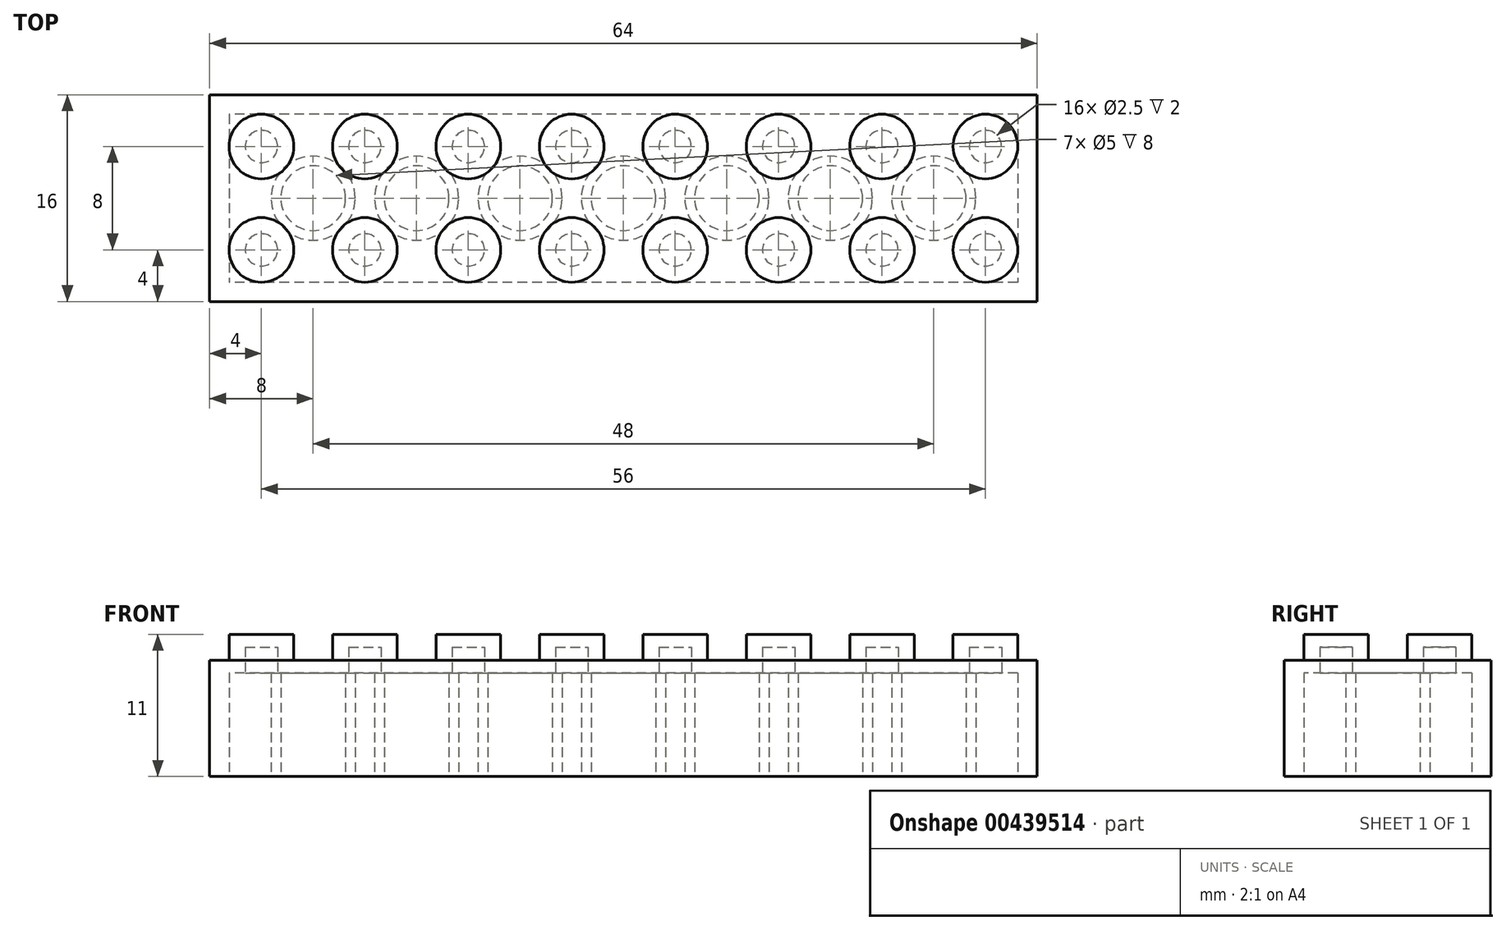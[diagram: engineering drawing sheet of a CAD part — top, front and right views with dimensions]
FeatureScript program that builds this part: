
annotation { "Feature Type Name" : "Feature", "Feature Type Description" : "" }
export const myFeature = defineFeature(function(context is Context, id is Id, definition is map)
    precondition{}
    {
        {
            var Q0;
            Q0=qCreatedBy(makeId("Top.planeOp"),FACE);
            var sketch = newSketch(context, id + "F0", { "sketchPlane" : qUnion([Q0])});
            skLineSegment(sketch, "E0.bottom", {"start": v(32, -8) * mm, "end": v(-32, -8) * mm});
            skLineSegment(sketch, "E0.top", {"start": v(32, 8) * mm, "end": v(-32, 8) * mm});
            skLineSegment(sketch, "E0.left", {"start": v(32, -8) * mm, "end": v(32, 8) * mm});
            skLineSegment(sketch, "E0.right", {"start": v(-32, -8) * mm, "end": v(-32, 8) * mm});
            skPoint(sketch, "E0.middle", {"position": v(0, 0) * mm});
            skSolve(sketch);
        }
        {
            var Q0;
            Q0=makeQuery(id+"F0.imprint","IMPRINT",FACE,{"disambiguationData":[TD([[makeQuery(id+"F0.imprint","IMPRINT",EDGE,{"derivedFrom":sQuery(id+"F0.wireOp",EDGE,"E0.bottom")}),-1.0]])]});
            extrude(context, id + "F1", {"entities" : qUnion([Q0]), "depth" : 9 * mm});
        }
        {
            var Q0;
            Q0=makeQuery(id+"F1.opExtrude","CAP_FACE",FACE,{"disambiguationData":[OSD([sQuery(id+"F0.wireOp",EDGE,"E0.bottom"),sQuery(id+"F0.wireOp",EDGE,"E0.top"),sQuery(id+"F0.wireOp",EDGE,"E0.left"),sQuery(id+"F0.wireOp",EDGE,"E0.right")])],"isStart":false});
            var sketch = newSketch(context, id + "F2", { "sketchPlane" : qUnion([Q0])});
            skCircle(sketch, "E1", {"center": v(-28, 4) * mm, "radius": 2.5 * mm});
            skCircle(sketch, "E2.0.1.0", {"center": v(-28, -4) * mm, "radius": 2.5 * mm});
            skCircle(sketch, "E2.1.0.0", {"center": v(-20, 4) * mm, "radius": 2.5 * mm});
            skCircle(sketch, "E2.1.1.0", {"center": v(-20, -4) * mm, "radius": 2.5 * mm});
            skCircle(sketch, "E2.2.0.0", {"center": v(-12, 4) * mm, "radius": 2.5 * mm});
            skCircle(sketch, "E2.2.1.0", {"center": v(-12, -4) * mm, "radius": 2.5 * mm});
            skCircle(sketch, "E2.3.0.0", {"center": v(-4, 4) * mm, "radius": 2.5 * mm});
            skCircle(sketch, "E2.3.1.0", {"center": v(-4, -4) * mm, "radius": 2.5 * mm});
            skCircle(sketch, "E2.4.0.0", {"center": v(4, 4) * mm, "radius": 2.5 * mm});
            skCircle(sketch, "E2.4.1.0", {"center": v(4, -4) * mm, "radius": 2.5 * mm});
            skCircle(sketch, "E2.5.0.0", {"center": v(12, 4) * mm, "radius": 2.5 * mm});
            skCircle(sketch, "E2.5.1.0", {"center": v(12, -4) * mm, "radius": 2.5 * mm});
            skCircle(sketch, "E2.6.0.0", {"center": v(20, 4) * mm, "radius": 2.5 * mm});
            skCircle(sketch, "E2.6.1.0", {"center": v(20, -4) * mm, "radius": 2.5 * mm});
            skCircle(sketch, "E2.7.0.0", {"center": v(28, 4) * mm, "radius": 2.5 * mm});
            skCircle(sketch, "E2.7.1.0", {"center": v(28, -4) * mm, "radius": 2.5 * mm});
            skLineSegment(sketch, "E2.direction1", {"start": v(-28, 4) * mm, "end": v(-20, 4) * mm, "construction": true});
            skLineSegment(sketch, "E2.direction2", {"start": v(-28, 4) * mm, "end": v(-28, -4) * mm, "construction": true});
            skSolve(sketch);
        }
        {
            var Q0;
            Q0 = qSketchRegion(id + "F2", true);
            extrude(context, id + "F3", {"entities" : qUnion([Q0]), "operationType" : NewBodyOperationType.ADD, "depth" : 2 * mm});
        }
        {
            var Q0;
            Q0=makeQuery(id+"F1.opExtrude","CAP_FACE",FACE,{"disambiguationData":[OSD([sQuery(id+"F0.wireOp",EDGE,"E0.bottom"),sQuery(id+"F0.wireOp",EDGE,"E0.top"),sQuery(id+"F0.wireOp",EDGE,"E0.left"),sQuery(id+"F0.wireOp",EDGE,"E0.right")])],"isStart":true});
            var sketch = newSketch(context, id + "F4", { "sketchPlane" : qUnion([Q0])});
            skLineSegment(sketch, "E3.bottom", {"start": v(30.5, -6.5) * mm, "end": v(-30.5, -6.5) * mm});
            skLineSegment(sketch, "E3.top", {"start": v(30.5, 6.5) * mm, "end": v(-30.5, 6.5) * mm});
            skLineSegment(sketch, "E3.left", {"start": v(30.5, -6.5) * mm, "end": v(30.5, 6.5) * mm});
            skLineSegment(sketch, "E3.right", {"start": v(-30.5, -6.5) * mm, "end": v(-30.5, 6.5) * mm});
            skPoint(sketch, "E3.middle", {"position": v(0, 0) * mm});
            skCircle(sketch, "E4", {"center": v(-24, 0) * mm, "radius": 3.25 * mm});
            skCircle(sketch, "E5", {"center": v(-24, 0) * mm, "radius": 2.5 * mm});
            skCircle(sketch, "E6.1.0.0", {"center": v(-16, 0) * mm, "radius": 3.25 * mm});
            skCircle(sketch, "E6.1.0.1", {"center": v(-16, 0) * mm, "radius": 2.5 * mm});
            skCircle(sketch, "E6.2.0.0", {"center": v(-8, 0) * mm, "radius": 3.25 * mm});
            skCircle(sketch, "E6.2.0.1", {"center": v(-8, 0) * mm, "radius": 2.5 * mm});
            skCircle(sketch, "E6.3.0.0", {"center": v(0, 0) * mm, "radius": 3.25 * mm});
            skCircle(sketch, "E6.3.0.1", {"center": v(0, 0) * mm, "radius": 2.5 * mm});
            skCircle(sketch, "E6.4.0.0", {"center": v(8, 0) * mm, "radius": 3.25 * mm});
            skCircle(sketch, "E6.4.0.1", {"center": v(8, 0) * mm, "radius": 2.5 * mm});
            skCircle(sketch, "E6.5.0.0", {"center": v(16, 0) * mm, "radius": 3.25 * mm});
            skCircle(sketch, "E6.5.0.1", {"center": v(16, 0) * mm, "radius": 2.5 * mm});
            skCircle(sketch, "E6.6.0.0", {"center": v(24, 0) * mm, "radius": 3.25 * mm});
            skCircle(sketch, "E6.6.0.1", {"center": v(24, 0) * mm, "radius": 2.5 * mm});
            skLineSegment(sketch, "E6.direction1", {"start": v(-24, 0) * mm, "end": v(-16, 0) * mm, "construction": true});
            skSolve(sketch);
        }
        {
            var Q0;
            Q0 = qSketchRegion(id + "F4", true);
            var Q1;
            Q1=makeQuery(id+"F4.imprint","IMPRINT",FACE,{"disambiguationData":[TD([[makeQuery(id+"F4.imprint","IMPRINT",EDGE,{"derivedFrom":sQuery(id+"F4.wireOp",EDGE,"E5")}),1.0]])]});
            var Q2;
            Q2=makeQuery(id+"F4.imprint","IMPRINT",FACE,{"disambiguationData":[TD([[makeQuery(id+"F4.imprint","IMPRINT",EDGE,{"derivedFrom":sQuery(id+"F4.wireOp",EDGE,"E6.1.0.1")}),1.0]])]});
            var Q3;
            Q3=makeQuery(id+"F4.imprint","IMPRINT",FACE,{"disambiguationData":[TD([[makeQuery(id+"F4.imprint","IMPRINT",EDGE,{"derivedFrom":sQuery(id+"F4.wireOp",EDGE,"E6.2.0.1")}),1.0]])]});
            var Q4;
            Q4=makeQuery(id+"F4.imprint","IMPRINT",FACE,{"disambiguationData":[TD([[makeQuery(id+"F4.imprint","IMPRINT",EDGE,{"derivedFrom":sQuery(id+"F4.wireOp",EDGE,"E6.3.0.1")}),1.0]])]});
            var Q5;
            Q5=makeQuery(id+"F4.imprint","IMPRINT",FACE,{"disambiguationData":[TD([[makeQuery(id+"F4.imprint","IMPRINT",EDGE,{"derivedFrom":sQuery(id+"F4.wireOp",EDGE,"E6.4.0.1")}),1.0]])]});
            var Q6;
            Q6=makeQuery(id+"F4.imprint","IMPRINT",FACE,{"disambiguationData":[TD([[makeQuery(id+"F4.imprint","IMPRINT",EDGE,{"derivedFrom":sQuery(id+"F4.wireOp",EDGE,"E6.5.0.1")}),1.0]])]});
            var Q7;
            Q7=makeQuery(id+"F4.imprint","IMPRINT",FACE,{"disambiguationData":[TD([[makeQuery(id+"F4.imprint","IMPRINT",EDGE,{"derivedFrom":sQuery(id+"F4.wireOp",EDGE,"E6.6.0.1")}),1.0]])]});
            extrude(context, id + "F5", {"entities" : qUnion([Q0, Q1, Q2, Q3, Q4, Q5, Q6, Q7]), "operationType" : NewBodyOperationType.REMOVE, "oppositeDirection" : true, "depth" : 8 * mm});
        }
        {
            var Q0;
            {var subQ0=sQuery(id+"F0.wireOp",EDGE,"E0.left");var subQ1=sQuery(id+"F0.wireOp",EDGE,"E0.top");var subQ2=sQuery(id+"F0.wireOp",EDGE,"E0.right");var subQ3=sQuery(id+"F0.wireOp",EDGE,"E0.bottom");Q0=makeQuery(id+"F5.boolean.opBoolean","SPLIT",FACE,{"disambiguationData":[TD([makeQuery(id+"F1.opExtrude","SWEPT_FACE",FACE,{"disambiguationData":[OSD([subQ3])]})])],"derivedFrom":makeQuery(id+"F1.opExtrude","CAP_FACE",FACE,{"disambiguationData":[OSD([subQ3,subQ1,subQ0,subQ2])],"isStart":true})});}
            var sketch = newSketch(context, id + "F6", { "sketchPlane" : qUnion([Q0])});
            skCircle(sketch, "E7", {"center": v(-28, 4) * mm, "radius": 1.25 * mm});
            skCircle(sketch, "E8.0.1.0", {"center": v(-28, -4) * mm, "radius": 1.25 * mm});
            skCircle(sketch, "E8.1.0.0", {"center": v(-20, 4) * mm, "radius": 1.25 * mm});
            skCircle(sketch, "E8.1.1.0", {"center": v(-20, -4) * mm, "radius": 1.25 * mm});
            skCircle(sketch, "E8.2.0.0", {"center": v(-12, 4) * mm, "radius": 1.25 * mm});
            skCircle(sketch, "E8.2.1.0", {"center": v(-12, -4) * mm, "radius": 1.25 * mm});
            skCircle(sketch, "E8.3.0.0", {"center": v(-4, 4) * mm, "radius": 1.25 * mm});
            skCircle(sketch, "E8.3.1.0", {"center": v(-4, -4) * mm, "radius": 1.25 * mm});
            skCircle(sketch, "E8.4.0.0", {"center": v(4, 4) * mm, "radius": 1.25 * mm});
            skCircle(sketch, "E8.4.1.0", {"center": v(4, -4) * mm, "radius": 1.25 * mm});
            skCircle(sketch, "E8.5.0.0", {"center": v(12, 4) * mm, "radius": 1.25 * mm});
            skCircle(sketch, "E8.5.1.0", {"center": v(12, -4) * mm, "radius": 1.25 * mm});
            skCircle(sketch, "E8.6.0.0", {"center": v(20, 4) * mm, "radius": 1.25 * mm});
            skCircle(sketch, "E8.6.1.0", {"center": v(20, -4) * mm, "radius": 1.25 * mm});
            skCircle(sketch, "E8.7.0.0", {"center": v(28, 4) * mm, "radius": 1.25 * mm});
            skCircle(sketch, "E8.7.1.0", {"center": v(28, -4) * mm, "radius": 1.25 * mm});
            skLineSegment(sketch, "E8.direction1", {"start": v(-28, 4) * mm, "end": v(-20, 4) * mm, "construction": true});
            skLineSegment(sketch, "E8.direction2", {"start": v(-28, 4) * mm, "end": v(-28, -4) * mm, "construction": true});
            skSolve(sketch);
        }
        {
            var Q0;
            Q0 = qSketchRegion(id + "F6", true);
            extrude(context, id + "F7", {"entities" : qUnion([Q0]), "operationType" : NewBodyOperationType.REMOVE, "oppositeDirection" : true, "depth" : 10 * mm});
        }
    });
